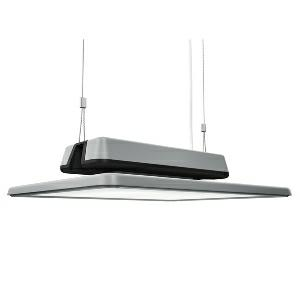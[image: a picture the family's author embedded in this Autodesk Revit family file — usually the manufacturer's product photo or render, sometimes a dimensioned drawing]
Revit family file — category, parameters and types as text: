
# Revit family: acaneo_-_hial_37000_850_n_dali_00804838_c446
name_source: partatom
category: Lighting Fixtures
units: mm (PartAtom-declared; Revit-internal decimal feet)

## family parameters
Cut with Voids When Loaded = No
Host = Face
Light Source = No
Part Type = Normal
Room Calculation Point = No
Round Connector Dimension = Use Diameter
Shared = No

## types (1)
- ACANEO - HIAL 37000/850/N/DALI (1 x LED, 40000 lm, 5000K)
    Apparent Load = 262 VA
    Approval mark = CE
    CIE Flux Codes = 84 97 100 100 100
    Color Rendering = 80-89
    Color Temperature = 5000K
    Control Gear = Electronic ballast
    Default Elevation = 1800 mm
    Description = HIAL 37000/850/N/DALI|High bay luminaire|light source: LED|work equipment: Adjustable electronic ballast, digital DALI|connected load: 220-240 V, 50/60 Hz|Power consumption: approx. 262 W|power factor: approx. 0,981|luminous flux: 40000 lm|luminous efficacy: 152 lm/W|colour temperature: Cold white, ca. 5000 K|color rendering index (CRI): >= 80|chromaticity tolerance:  3 SDCM|System of protection: IP 65|class of protection: I|technology: Continuously dimmable|luminaire body|material: Aluminium|surface: Powder coatet|colour: White aluminium|lamp cover: Acrylic (PMMA), Clear|weight (net): approx. 10.8 kg|mains lead: Built-in plug RST 20i5 Einbau|Fastening: Available separately|Accessory: Junction box (RST 20i5)|minimum ambient temperature: -30 ░C|maximum ambient temperature: 50 ░C|glare control: Optics|unified glare rating(4H 8H): <=  22|
    Frequency = 50 Hz, 60 Hz
    Height = 125 mm
    Lamp = 1 x LED
    Lamp Light Flux = 40000 lm
    Lamp count = 1
    Length = 585 mm
    Luminous efficacy = 153 lm/W
    Manufacturer = Waldmann
    ModVariant = No
    Model = 00804838
    Mounting Place = Ceiling
    Mounting Type = Pendant
    Number of Poles = 1
    OnlyDefault = Yes
    Power Factor = 1
    Product Name = ACANEO - HIAL 37000/850/N/DALI
    Product group = High bay luminaire (industry)
    ProductGroupID = 901
    Protection Class = Protection class I
    Protection Degree = IP 65
    RLX_Detail_Level = 1
    RLX_Emergency_Light_Flux = 0 lm
    RLX_Emergency_Type = 0
    RLX_Emergency_Type_DB = No
    RlxData = <blob elided: 29869 chars, md5=38aa6d3f>
    Socket = socket
    Standby Power = 0 W
    System Light Flux = 40000 lm
    System Power = 262 W
    Type Comments = Product without accessories
    Type Image = acaneo-hial.jpg
    URL = http://relux.com
    VarID = ---
    Voltage = 230 V
    Voltage Range = 110-120 V, 220-240 V
    Weight = 0.00 kg
    Width = 480 mm

## geometry (parser evidence)
native form markers: Blend x4, Sweep x9
no freeform markers — native parametric forms only
